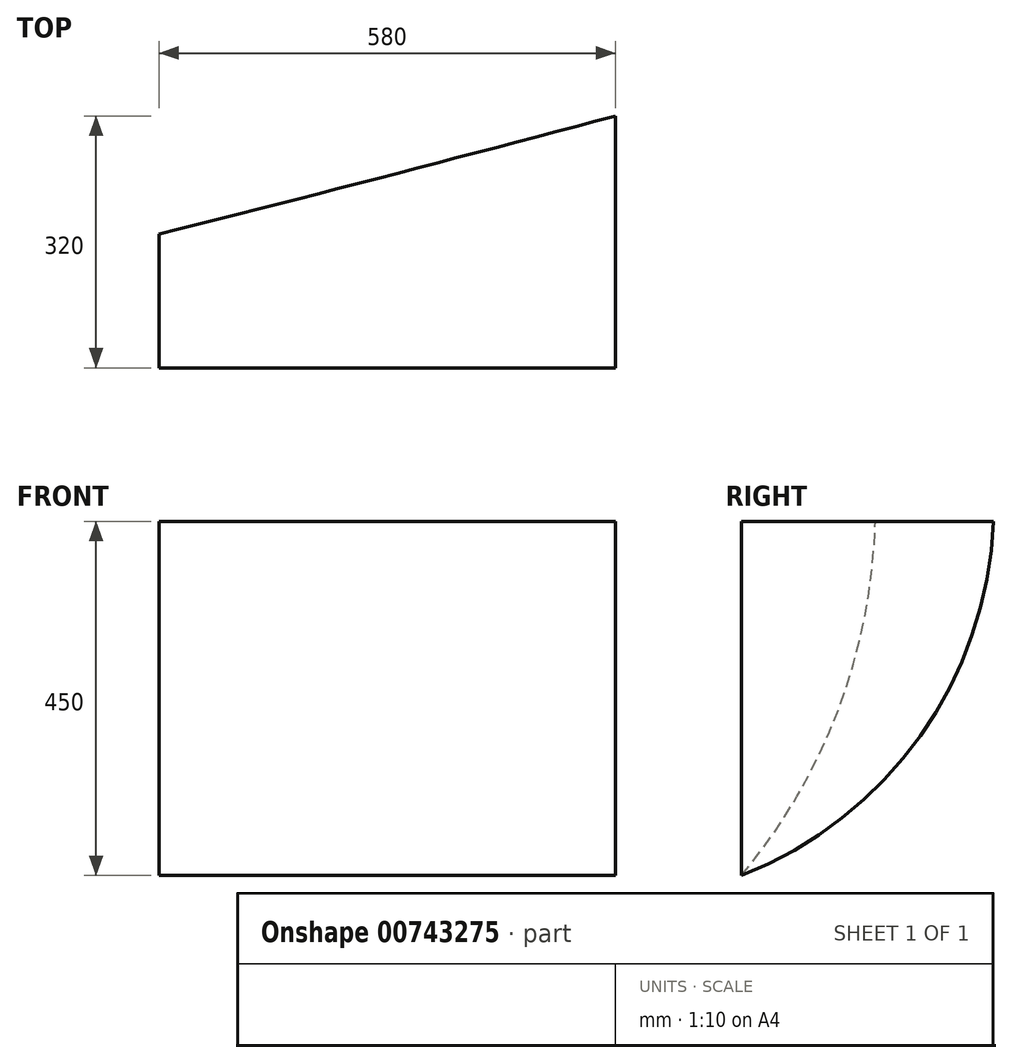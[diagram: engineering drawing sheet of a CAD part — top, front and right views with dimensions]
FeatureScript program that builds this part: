
annotation { "Feature Type Name" : "Feature", "Feature Type Description" : "" }
export const myFeature = defineFeature(function(context is Context, id is Id, definition is map)
    precondition{}
    {
        {
            var Q0;
            Q0=qCreatedBy(makeId("Right.planeOp"),FACE);
            var sketch = newSketch(context, id + "F0", { "sketchPlane" : qUnion([Q0])});
            skLineSegment(sketch, "E0", {"start": v(0, 0) * mm, "end": v(0, 450) * mm});
            skLineSegment(sketch, "E1", {"start": v(0, 450) * mm, "end": v(320, 450) * mm});
            skArc(sketch, "E2", {"start": v(0, 0) * mm, "mid": v(226.96, 177.38) * mm, "end": v(320, 450) * mm});
            skSolve(sketch);
        }
        {
            var Q0;
            Q0=qCreatedBy(makeId("Right.planeOp"),FACE);
            cPlane(context, id + "F1", {"entities" : qUnion([Q0]), "cplaneType" : CPlaneType.OFFSET, "offset" : 580 * mm, "oppositeDirection" : true, "width" : 150 * mm, "height" : 150 * mm});
        }
        {
            var Q0;
            Q0=qCreatedBy(id+"F1.planeOp",FACE);
            var sketch = newSketch(context, id + "F2", { "sketchPlane" : qUnion([Q0])});
            skLineSegment(sketch, "E3", {"start": v(0, 0) * mm, "end": v(0, 450) * mm});
            skLineSegment(sketch, "E4", {"start": v(0, 450) * mm, "end": v(170, 450) * mm});
            skArc(sketch, "E5", {"start": v(0, 0) * mm, "mid": v(122.92, 210.67) * mm, "end": v(170, 450) * mm});
            skSolve(sketch);
        }
        {
            var Q0;
            Q0=qCreatedBy(id+"F1.planeOp",FACE);
            cPlane(context, id + "F3", {"entities" : qUnion([Q0]), "cplaneType" : CPlaneType.OFFSET, "offset" : 80 * mm, "width" : 150 * mm, "height" : 150 * mm});
        }
        {
            var Q0;
            Q0=qCreatedBy(id+"F3.planeOp",FACE);
            var sketch = newSketch(context, id + "F4", { "sketchPlane" : qUnion([Q0])});
            skLineSegment(sketch, "E6", {"start": v(0, 0) * mm, "end": v(0, 450) * mm});
            skLineSegment(sketch, "E7", {"start": v(0, 450) * mm, "end": v(190, 450) * mm});
            skArc(sketch, "E8", {"start": v(0, 0) * mm, "mid": v(137.1, 207.23) * mm, "end": v(190, 450) * mm});
            skSolve(sketch);
        }
        {
            var Q0;
            Q0=makeQuery(id+"F0.imprint","IMPRINT",FACE,{"disambiguationData":[TD([[makeQuery(id+"F0.imprint","IMPRINT",EDGE,{"derivedFrom":sQuery(id+"F0.wireOp",EDGE,"E0")}),-1.0]])]});
            var Q1;
            Q1=makeQuery(id+"F4.imprint","IMPRINT",FACE,{"disambiguationData":[TD([[makeQuery(id+"F4.imprint","IMPRINT",EDGE,{"derivedFrom":sQuery(id+"F4.wireOp",EDGE,"E6")}),-1.0]])]});
            var Q2;
            Q2=makeQuery(id+"F2.imprint","IMPRINT",FACE,{"disambiguationData":[TD([[makeQuery(id+"F2.imprint","IMPRINT",EDGE,{"derivedFrom":sQuery(id+"F2.wireOp",EDGE,"E3")}),-1.0]])]});
            loft(context, id + "F5", {"sheetProfilesArray" : [{ "sheetProfileEntities" : qUnion([Q0]) }, { "sheetProfileEntities" : qUnion([Q1]) }, { "sheetProfileEntities" : qUnion([Q2]) }]});
        }
    });
